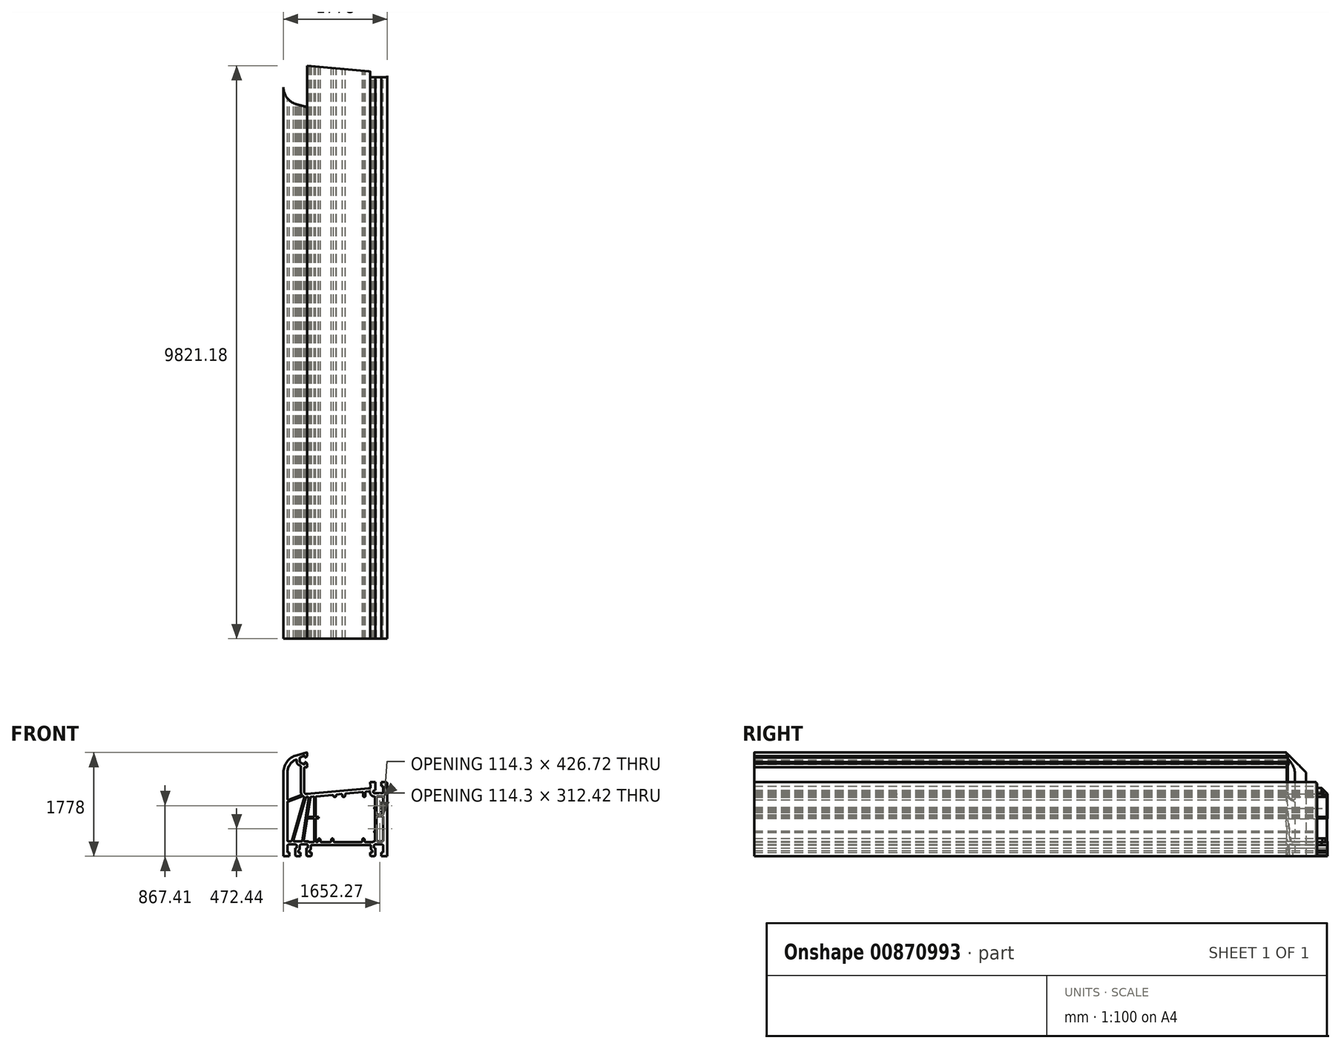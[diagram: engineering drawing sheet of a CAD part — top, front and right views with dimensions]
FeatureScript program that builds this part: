
annotation { "Feature Type Name" : "Feature", "Feature Type Description" : "" }
export const myFeature = defineFeature(function(context is Context, id is Id, definition is map)
    precondition{}
    {
        {
            var Q0;
            Q0=qCreatedBy(makeId("Front.planeOp"),FACE);
            var sketch = newSketch(context, id + "F0", { "sketchPlane" : qUnion([Q0])});
            skLineSegment(sketch, "E0", {"start": v(-889, -889) * mm, "end": v(-787.4, -889) * mm});
            skLineSegment(sketch, "E1", {"start": v(-508, 723.9) * mm, "end": v(-520.7, 723.9) * mm});
            skLineSegment(sketch, "E2", {"start": v(-520.7, 723.9) * mm, "end": v(-520.7, 701.04) * mm});
            skLineSegment(sketch, "E3", {"start": v(787.4, -889) * mm, "end": v(889, -889) * mm});
            skLineSegment(sketch, "E4", {"start": v(889, -889) * mm, "end": v(889, 355.6) * mm});
            skLineSegment(sketch, "E5", {"start": v(863.6, 381) * mm, "end": v(787.4, 381) * mm});
            skLineSegment(sketch, "E6", {"start": v(787.4, 381) * mm, "end": v(787.4, 314.96) * mm});
            skLineSegment(sketch, "E7", {"start": v(673.1, 241.3) * mm, "end": v(685.8, 241.3) * mm});
            skLineSegment(sketch, "E8", {"start": v(685.8, 241.3) * mm, "end": v(685.8, 381) * mm});
            skLineSegment(sketch, "E9", {"start": v(685.8, 381) * mm, "end": v(596.9, 381) * mm});
            skLineSegment(sketch, "E10", {"start": v(-889, 548.53) * mm, "end": v(-889, -889) * mm});
            skLineSegment(sketch, "E11", {"start": v(-482.6, 698.5) * mm, "end": v(-508, 723.9) * mm});
            skLineSegment(sketch, "E12", {"start": v(-482.6, 647.7) * mm, "end": v(-482.6, 698.5) * mm});
            skLineSegment(sketch, "E13", {"start": v(-520.7, 635) * mm, "end": v(-495.3, 635) * mm});
            skLineSegment(sketch, "E14", {"start": v(-589.28, 648.94) * mm, "end": v(-589.28, 635) * mm});
            skLineSegment(sketch, "E15", {"start": v(-623.74, 673.1) * mm, "end": v(-596.61, 660.45) * mm});
            skLineSegment(sketch, "E16", {"start": v(-660.4, 753.62) * mm, "end": v(-660.4, 730.65) * mm});
            skLineSegment(sketch, "E17", {"start": v(-820.42, 91.47) * mm, "end": v(-820.42, 548.53) * mm});
            skLineSegment(sketch, "E18", {"start": v(-812.06, 49.34) * mm, "end": v(-561.15, 140.67) * mm});
            skLineSegment(sketch, "E19", {"start": v(-820.42, -617.22) * mm, "end": v(-820.42, 37.41) * mm});
            skLineSegment(sketch, "E20", {"start": v(-587.31, 158.18) * mm, "end": v(-803.38, 79.54) * mm});
            skLineSegment(sketch, "E21", {"start": v(820.42, -215.9) * mm, "end": v(820.42, -617.22) * mm});
            skLineSegment(sketch, "E22", {"start": v(718.82, -203.2) * mm, "end": v(807.72, -203.2) * mm});
            skLineSegment(sketch, "E23", {"start": v(706.12, -617.22) * mm, "end": v(706.12, -215.9) * mm});
            skLineSegment(sketch, "E24", {"start": v(680.72, -495.3) * mm, "end": v(680.72, -618.92) * mm});
            skLineSegment(sketch, "E25", {"start": v(665.48, -482.6) * mm, "end": v(668.02, -482.6) * mm});
            skLineSegment(sketch, "E26", {"start": v(665.48, -457.2) * mm, "end": v(665.48, -482.6) * mm});
            skLineSegment(sketch, "E27", {"start": v(668.02, -457.2) * mm, "end": v(665.48, -457.2) * mm});
            skLineSegment(sketch, "E28", {"start": v(680.72, -88.9) * mm, "end": v(680.72, -444.5) * mm});
            skLineSegment(sketch, "E29", {"start": v(665.48, -76.2) * mm, "end": v(668.02, -76.2) * mm});
            skLineSegment(sketch, "E30", {"start": v(665.48, -50.8) * mm, "end": v(665.48, -76.2) * mm});
            skLineSegment(sketch, "E31", {"start": v(668.02, -50.8) * mm, "end": v(665.48, -50.8) * mm});
            skLineSegment(sketch, "E32", {"start": v(680.72, 122.06) * mm, "end": v(680.72, -38.1) * mm});
            skLineSegment(sketch, "E33", {"start": v(706.12, -165.1) * mm, "end": v(706.12, 121.92) * mm});
            skLineSegment(sketch, "E34", {"start": v(807.72, -177.8) * mm, "end": v(718.82, -177.8) * mm});
            skLineSegment(sketch, "E35", {"start": v(820.42, -152.4) * mm, "end": v(820.42, -165.1) * mm});
            skLineSegment(sketch, "E36", {"start": v(787.4, -139.7) * mm, "end": v(807.72, -139.7) * mm});
            skLineSegment(sketch, "E37", {"start": v(787.4, -114.3) * mm, "end": v(787.4, -139.7) * mm});
            skLineSegment(sketch, "E38", {"start": v(807.72, -114.3) * mm, "end": v(787.4, -114.3) * mm});
            skLineSegment(sketch, "E39", {"start": v(787.4, -88.9) * mm, "end": v(807.72, -88.9) * mm});
            skLineSegment(sketch, "E40", {"start": v(787.4, -63.5) * mm, "end": v(787.4, -88.9) * mm});
            skLineSegment(sketch, "E41", {"start": v(807.72, -63.5) * mm, "end": v(787.4, -63.5) * mm});
            skLineSegment(sketch, "E42", {"start": v(820.42, 121.92) * mm, "end": v(820.42, -50.8) * mm});
            skLineSegment(sketch, "E43", {"start": v(820.42, 314.96) * mm, "end": v(820.42, 215.9) * mm});
            skLineSegment(sketch, "E44", {"start": v(787.4, 314.96) * mm, "end": v(820.42, 314.96) * mm});
            skLineSegment(sketch, "E45", {"start": v(-520.7, 822.96) * mm, "end": v(-520.7, 800.1) * mm});
            skLineSegment(sketch, "E46", {"start": v(-602.27, 804.86) * mm, "end": v(-538.77, 834.47) * mm});
            skLineSegment(sketch, "E47", {"start": v(-609.6, 730.65) * mm, "end": v(-609.6, 793.35) * mm});
            skLineSegment(sketch, "E48", {"start": v(-538.77, 689.53) * mm, "end": v(-602.27, 719.14) * mm});
            skLineSegment(sketch, "E49", {"start": v(787.4, -822.96) * mm, "end": v(787.4, -889) * mm});
            skLineSegment(sketch, "E50", {"start": v(820.42, -822.96) * mm, "end": v(787.4, -822.96) * mm});
            skLineSegment(sketch, "E51", {"start": v(820.42, -711.2) * mm, "end": v(820.42, -822.96) * mm});
            skLineSegment(sketch, "E52", {"start": v(525.87, 217.04) * mm, "end": v(578.17, 221.93) * mm});
            skLineSegment(sketch, "E53", {"start": v(179.16, 184.6) * mm, "end": v(462.37, 211.1) * mm});
            skLineSegment(sketch, "E54", {"start": v(26.4, 170.31) * mm, "end": v(102.96, 177.48) * mm});
            skLineSegment(sketch, "E55", {"start": v(-323.76, 137.56) * mm, "end": v(-49.4, 163.22) * mm});
            skLineSegment(sketch, "E56", {"start": v(-417.58, 128.78) * mm, "end": v(-374.56, 132.8) * mm});
            skLineSegment(sketch, "E57", {"start": v(-486.55, 122.33) * mm, "end": v(-469.67, 123.9) * mm});
            skLineSegment(sketch, "E58", {"start": v(-589.28, 635) * mm, "end": v(-589.28, 215.9) * mm});
            skLineSegment(sketch, "E59", {"start": v(-533.4, 215.9) * mm, "end": v(-533.4, 622.3) * mm});
            skLineSegment(sketch, "E60", {"start": v(572.97, 277.57) * mm, "end": v(-491.75, 177.97) * mm});
            skLineSegment(sketch, "E61", {"start": v(795.02, 190.5) * mm, "end": v(673.1, 190.5) * mm});
            skLineSegment(sketch, "E62", {"start": v(718.82, 134.62) * mm, "end": v(807.72, 134.62) * mm});
            skLineSegment(sketch, "E63", {"start": v(-360.68, -248.92) * mm, "end": v(-360.68, -629.92) * mm});
            skLineSegment(sketch, "E64", {"start": v(-470.96, -236.22) * mm, "end": v(-373.38, -236.22) * mm});
            skLineSegment(sketch, "E65", {"start": v(-538.56, -615.34) * mm, "end": v(-483.52, -247.04) * mm});
            skLineSegment(sketch, "E66", {"start": v(-455.93, 109.39) * mm, "end": v(-564.8, -619.1) * mm});
            skLineSegment(sketch, "E67", {"start": v(-476.68, -201.32) * mm, "end": v(-428.96, 118.01) * mm});
            skLineSegment(sketch, "E68", {"start": v(-373.38, -215.9) * mm, "end": v(-464.12, -215.9) * mm});
            skLineSegment(sketch, "E69", {"start": v(-360.68, 120.16) * mm, "end": v(-360.68, -203.2) * mm});
            skLineSegment(sketch, "E70", {"start": v(-335.28, -203.2) * mm, "end": v(-335.28, 124.91) * mm});
            skLineSegment(sketch, "E71", {"start": v(-284.48, -215.9) * mm, "end": v(-322.58, -215.9) * mm});
            skLineSegment(sketch, "E72", {"start": v(-284.48, -241.3) * mm, "end": v(-284.48, -215.9) * mm});
            skLineSegment(sketch, "E73", {"start": v(-322.58, -241.3) * mm, "end": v(-284.48, -241.3) * mm});
            skLineSegment(sketch, "E74", {"start": v(-335.28, -629.92) * mm, "end": v(-335.28, -254) * mm});
            skLineSegment(sketch, "E75", {"start": v(167.64, 152.4) * mm, "end": v(167.64, 171.96) * mm});
            skLineSegment(sketch, "E76", {"start": v(116.84, 164.83) * mm, "end": v(116.84, 152.4) * mm});
            skLineSegment(sketch, "E77", {"start": v(593.11, 279.46) * mm, "end": v(572.97, 277.57) * mm});
            skLineSegment(sketch, "E78", {"start": v(604.58, 293.2) * mm, "end": v(596.9, 381) * mm});
            skLineSegment(sketch, "E79", {"start": v(-482.6, 825.5) * mm, "end": v(-482.6, 881.38) * mm});
            skLineSegment(sketch, "E80", {"start": v(-508, 800.1) * mm, "end": v(-482.6, 825.5) * mm});
            skLineSegment(sketch, "E81", {"start": v(-520.7, 800.1) * mm, "end": v(-508, 800.1) * mm});
            skLineSegment(sketch, "E82", {"start": v(-406.4, -876.3) * mm, "end": v(-406.4, -822.96) * mm});
            skLineSegment(sketch, "E83", {"start": v(-406.4, -822.96) * mm, "end": v(-444.5, -822.96) * mm});
            skLineSegment(sketch, "E84", {"start": v(-444.5, -822.96) * mm, "end": v(-444.5, -793.3) * mm});
            skLineSegment(sketch, "E85", {"start": v(-419.1, -749.3) * mm, "end": v(-419.1, -711.2) * mm});
            skLineSegment(sketch, "E86", {"start": v(-495.3, -876.3) * mm, "end": v(-482.6, -889) * mm});
            skLineSegment(sketch, "E87", {"start": v(-660.4, -749.3) * mm, "end": v(-685.8, -749.3) * mm});
            skLineSegment(sketch, "E88", {"start": v(-685.8, -749.3) * mm, "end": v(-685.8, -876.3) * mm});
            skLineSegment(sketch, "E89", {"start": v(-685.8, -876.3) * mm, "end": v(-673.1, -889) * mm});
            skLineSegment(sketch, "E90", {"start": v(-673.1, -889) * mm, "end": v(-596.9, -889) * mm});
            skLineSegment(sketch, "E91", {"start": v(-596.9, -889) * mm, "end": v(-596.9, -822.96) * mm});
            skLineSegment(sketch, "E92", {"start": v(-596.9, -822.96) * mm, "end": v(-635, -822.96) * mm});
            skLineSegment(sketch, "E93", {"start": v(-635, -822.96) * mm, "end": v(-635, -793.3) * mm});
            skLineSegment(sketch, "E94", {"start": v(-609.6, -749.3) * mm, "end": v(-609.6, -711.2) * mm});
            skLineSegment(sketch, "E95", {"start": v(-660.4, -711.2) * mm, "end": v(-660.4, -749.3) * mm});
            skLineSegment(sketch, "E96", {"start": v(596.9, -822.96) * mm, "end": v(596.9, -876.3) * mm});
            skLineSegment(sketch, "E97", {"start": v(635, -822.96) * mm, "end": v(596.9, -822.96) * mm});
            skLineSegment(sketch, "E98", {"start": v(635, -793.3) * mm, "end": v(635, -822.96) * mm});
            skLineSegment(sketch, "E99", {"start": v(609.6, -711.2) * mm, "end": v(609.6, -749.3) * mm});
            skLineSegment(sketch, "E100", {"start": v(-257.8, -629.92) * mm, "end": v(-257.8, -603.25) * mm});
            skLineSegment(sketch, "E101", {"start": v(-295.9, -603.25) * mm, "end": v(-295.9, -629.92) * mm});
            skLineSegment(sketch, "E102", {"start": v(-31.75, -629.92) * mm, "end": v(-31.75, -603.25) * mm});
            skLineSegment(sketch, "E103", {"start": v(-69.85, -603.25) * mm, "end": v(-69.85, -629.92) * mm});
            skLineSegment(sketch, "E104", {"start": v(499.11, -629.92) * mm, "end": v(499.11, -603.25) * mm});
            skLineSegment(sketch, "E105", {"start": v(461.01, -603.25) * mm, "end": v(461.01, -629.92) * mm});
            skLineSegment(sketch, "E106", {"start": v(-495.3, -749.3) * mm, "end": v(-495.3, -876.3) * mm});
            skLineSegment(sketch, "E107", {"start": v(-469.9, -749.3) * mm, "end": v(-495.3, -749.3) * mm});
            skLineSegment(sketch, "E108", {"start": v(-469.9, -711.2) * mm, "end": v(-469.9, -749.3) * mm});
            skLineSegment(sketch, "E109", {"start": v(-482.6, -889) * mm, "end": v(-419.1, -889) * mm});
            skLineSegment(sketch, "E110", {"start": v(-419.1, -889) * mm, "end": v(-406.4, -876.3) * mm});
            skLineSegment(sketch, "E111", {"start": v(-820.42, -822.96) * mm, "end": v(-820.42, -711.2) * mm});
            skLineSegment(sketch, "E112", {"start": v(-787.4, -822.96) * mm, "end": v(-820.42, -822.96) * mm});
            skLineSegment(sketch, "E113", {"start": v(-787.4, -889) * mm, "end": v(-787.4, -822.96) * mm});
            skLineSegment(sketch, "E114", {"start": v(-492.2, 888.74) * mm, "end": v(-663.09, 842.95) * mm});
            skLineSegment(sketch, "E115", {"start": v(476.25, 198.46) * mm, "end": v(476.25, 146.05) * mm});
            skLineSegment(sketch, "E116", {"start": v(514.35, 146.05) * mm, "end": v(514.35, 204.4) * mm});
            skLineSegment(sketch, "E117", {"start": v(-718.23, -613.72) * mm, "end": v(-509.92, 112.75) * mm});
            skLineSegment(sketch, "E118", {"start": v(-534.56, 118.96) * mm, "end": v(-746.66, -620.72) * mm});
            skLineSegment(sketch, "E119", {"start": v(660.4, -749.3) * mm, "end": v(660.4, -711.2) * mm});
            skLineSegment(sketch, "E120", {"start": v(685.8, -749.3) * mm, "end": v(660.4, -749.3) * mm});
            skLineSegment(sketch, "E121", {"start": v(685.8, -876.3) * mm, "end": v(685.8, -749.3) * mm});
            skLineSegment(sketch, "E122", {"start": v(673.1, -889) * mm, "end": v(685.8, -876.3) * mm});
            skLineSegment(sketch, "E123", {"start": v(609.6, -889) * mm, "end": v(673.1, -889) * mm});
            skLineSegment(sketch, "E124", {"start": v(596.9, -876.3) * mm, "end": v(609.6, -889) * mm});
            skLineSegment(sketch, "E125", {"start": v(-758.87, -629.92) * mm, "end": v(-807.72, -629.92) * mm});
            skLineSegment(sketch, "E126", {"start": v(-577.36, -629.92) * mm, "end": v(-706.02, -629.92) * mm});
            skLineSegment(sketch, "E127", {"start": v(-495.3, -629.92) * mm, "end": v(-526, -629.92) * mm});
            skLineSegment(sketch, "E128", {"start": v(-373.38, -642.62) * mm, "end": v(-448.12, -642.62) * mm});
            skLineSegment(sketch, "E129", {"start": v(-308.6, -642.62) * mm, "end": v(-322.58, -642.62) * mm});
            skLineSegment(sketch, "E130", {"start": v(-82.55, -642.62) * mm, "end": v(-245.1, -642.62) * mm});
            skLineSegment(sketch, "E131", {"start": v(448.31, -642.62) * mm, "end": v(-19.05, -642.62) * mm});
            skLineSegment(sketch, "E132", {"start": v(638.62, -642.62) * mm, "end": v(511.81, -642.62) * mm});
            skLineSegment(sketch, "E133", {"start": v(807.72, -629.92) * mm, "end": v(718.82, -629.92) * mm});
            skLineSegment(sketch, "E134", {"start": v(685.8, -685.8) * mm, "end": v(795.02, -685.8) * mm});
            skLineSegment(sketch, "E135", {"start": v(-406.4, -698.5) * mm, "end": v(596.9, -698.5) * mm});
            skLineSegment(sketch, "E136", {"start": v(-584.2, -685.8) * mm, "end": v(-495.3, -685.8) * mm});
            skLineSegment(sketch, "E137", {"start": v(-795.02, -685.8) * mm, "end": v(-685.8, -685.8) * mm});
            skArc(sketch, "E138", {"start": v(-663.09, 842.95) * mm, "mid": v(-826.01, 734.09) * mm, "end": v(-889, 548.53) * mm});
            skArc(sketch, "E139", {"start": v(604.58, 293.2) * mm, "mid": v(601.68, 283.97) * mm, "end": v(593.11, 279.46) * mm});
            skArc(sketch, "E140", {"start": v(647.76, 214.11) * mm, "mid": v(654.52, 233.22) * mm, "end": v(673.1, 241.3) * mm});
            skArc(sketch, "E141", {"start": v(514.35, 204.4) * mm, "mid": v(517.66, 212.95) * mm, "end": v(525.87, 217.04) * mm});
            skArc(sketch, "E142", {"start": v(462.37, 211.1) * mm, "mid": v(472.1, 207.84) * mm, "end": v(476.25, 198.46) * mm});
            skArc(sketch, "E143", {"start": v(476.25, 146.05) * mm, "mid": v(495.3, 127) * mm, "end": v(514.35, 146.05) * mm});
            skArc(sketch, "E144", {"start": v(-49.4, 163.22) * mm, "mid": v(-39.9, 160.17) * mm, "end": v(-35.53, 151.19) * mm});
            skArc(sketch, "E145", {"start": v(15, 155.91) * mm, "mid": v(17.61, 165.55) * mm, "end": v(26.4, 170.31) * mm});
            skArc(sketch, "E146", {"start": v(-35.53, 151.19) * mm, "mid": v(-7.8, 127.11) * mm, "end": v(15, 155.91) * mm});
            skArc(sketch, "E147", {"start": v(-706.02, -629.92) * mm, "mid": v(-716.17, -624.86) * mm, "end": v(-718.23, -613.72) * mm});
            skArc(sketch, "E148", {"start": v(-509.92, 112.75) * mm, "mid": v(-505.24, 119.48) * mm, "end": v(-497.42, 121.94) * mm});
            skArc(sketch, "E149", {"start": v(-540.64, 133.58) * mm, "mid": v(-535.04, 127.33) * mm, "end": v(-534.56, 118.96) * mm});
            skArc(sketch, "E150", {"start": v(-746.66, -620.72) * mm, "mid": v(-751.23, -627.36) * mm, "end": v(-758.87, -629.92) * mm});
            skArc(sketch, "E151", {"start": v(660.4, -711.2) * mm, "mid": v(661.27, -704.63) * mm, "end": v(663.8, -698.5) * mm});
            skArc(sketch, "E152", {"start": v(609.6, -749.3) * mm, "mid": v(616.4, -774.7) * mm, "end": v(635, -793.3) * mm});
            skArc(sketch, "E153", {"start": v(596.9, -698.5) * mm, "mid": v(605.88, -702.22) * mm, "end": v(609.6, -711.2) * mm});
            skArc(sketch, "E154", {"start": v(-807.72, -629.92) * mm, "mid": v(-816.7, -626.2) * mm, "end": v(-820.42, -617.22) * mm});
            skArc(sketch, "E155", {"start": v(-454.5, -640.9) * mm, "mid": v(-474.17, -632.71) * mm, "end": v(-495.3, -629.92) * mm});
            skArc(sketch, "E156", {"start": v(-448.12, -642.62) * mm, "mid": v(-451.42, -642.18) * mm, "end": v(-454.5, -640.9) * mm});
            skArc(sketch, "E157", {"start": v(645, -640.9) * mm, "mid": v(641.92, -642.18) * mm, "end": v(638.62, -642.62) * mm});
            skArc(sketch, "E158", {"start": v(670.42, -631.39) * mm, "mid": v(657.3, -635.08) * mm, "end": v(645, -640.9) * mm});
            skArc(sketch, "E159", {"start": v(820.42, -617.22) * mm, "mid": v(816.7, -626.2) * mm, "end": v(807.72, -629.92) * mm});
            skArc(sketch, "E160", {"start": v(795.02, -685.8) * mm, "mid": v(812.98, -693.24) * mm, "end": v(820.42, -711.2) * mm});
            skArc(sketch, "E161", {"start": v(-495.3, -685.8) * mm, "mid": v(-482.6, -689.2) * mm, "end": v(-473.3, -698.5) * mm});
            skArc(sketch, "E162", {"start": v(-820.42, -711.2) * mm, "mid": v(-812.98, -693.24) * mm, "end": v(-795.02, -685.8) * mm});
            skArc(sketch, "E163", {"start": v(663.8, -698.5) * mm, "mid": v(673.1, -689.2) * mm, "end": v(685.8, -685.8) * mm});
            skArc(sketch, "E164", {"start": v(-69.85, -629.92) * mm, "mid": v(-73.57, -638.9) * mm, "end": v(-82.55, -642.62) * mm});
            skArc(sketch, "E165", {"start": v(-31.75, -603.25) * mm, "mid": v(-50.8, -584.2) * mm, "end": v(-69.85, -603.25) * mm});
            skArc(sketch, "E166", {"start": v(-19.05, -642.62) * mm, "mid": v(-28.03, -638.9) * mm, "end": v(-31.75, -629.92) * mm});
            skArc(sketch, "E167", {"start": v(-245.1, -642.62) * mm, "mid": v(-254.1, -638.9) * mm, "end": v(-257.8, -629.92) * mm});
            skArc(sketch, "E168", {"start": v(-257.8, -603.25) * mm, "mid": v(-276.86, -584.2) * mm, "end": v(-295.9, -603.25) * mm});
            skArc(sketch, "E169", {"start": v(-295.9, -629.92) * mm, "mid": v(-299.63, -638.9) * mm, "end": v(-308.6, -642.62) * mm});
            skArc(sketch, "E170", {"start": v(511.81, -642.62) * mm, "mid": v(502.83, -638.9) * mm, "end": v(499.11, -629.92) * mm});
            skArc(sketch, "E171", {"start": v(499.11, -603.25) * mm, "mid": v(480.06, -584.2) * mm, "end": v(461.01, -603.25) * mm});
            skArc(sketch, "E172", {"start": v(461.01, -629.92) * mm, "mid": v(457.3, -638.9) * mm, "end": v(448.31, -642.62) * mm});
            skArc(sketch, "E173", {"start": v(-473.3, -698.5) * mm, "mid": v(-470.77, -704.63) * mm, "end": v(-469.9, -711.2) * mm});
            skArc(sketch, "E174", {"start": v(-444.5, -793.3) * mm, "mid": v(-425.9, -774.7) * mm, "end": v(-419.1, -749.3) * mm});
            skArc(sketch, "E175", {"start": v(-419.1, -711.2) * mm, "mid": v(-415.38, -702.22) * mm, "end": v(-406.4, -698.5) * mm});
            skArc(sketch, "E176", {"start": v(-685.8, -685.8) * mm, "mid": v(-667.84, -693.24) * mm, "end": v(-660.4, -711.2) * mm});
            skArc(sketch, "E177", {"start": v(-635, -793.3) * mm, "mid": v(-616.4, -774.7) * mm, "end": v(-609.6, -749.3) * mm});
            skArc(sketch, "E178", {"start": v(-609.6, -711.2) * mm, "mid": v(-602.16, -693.24) * mm, "end": v(-584.2, -685.8) * mm});
            skArc(sketch, "E179", {"start": v(-482.6, 881.38) * mm, "mid": v(-485.58, 887.43) * mm, "end": v(-492.2, 888.74) * mm});
            skArc(sketch, "E180", {"start": v(-538.77, 834.47) * mm, "mid": v(-526.58, 833.67) * mm, "end": v(-520.7, 822.96) * mm});
            skArc(sketch, "E181", {"start": v(-609.6, 793.35) * mm, "mid": v(-607.61, 800.17) * mm, "end": v(-602.27, 804.86) * mm});
            skArc(sketch, "E182", {"start": v(-602.27, 719.14) * mm, "mid": v(-607.61, 723.83) * mm, "end": v(-609.6, 730.65) * mm});
            skArc(sketch, "E183", {"start": v(-520.7, 701.04) * mm, "mid": v(-526.58, 690.33) * mm, "end": v(-538.77, 689.53) * mm});
            skArc(sketch, "E184", {"start": v(-495.3, 635) * mm, "mid": v(-486.32, 638.72) * mm, "end": v(-482.6, 647.7) * mm});
            skArc(sketch, "E185", {"start": v(-596.61, 660.45) * mm, "mid": v(-591.27, 655.77) * mm, "end": v(-589.28, 648.94) * mm});
            skArc(sketch, "E186", {"start": v(-660.4, 730.65) * mm, "mid": v(-650.46, 696.53) * mm, "end": v(-623.74, 673.1) * mm});
            skArc(sketch, "E187", {"start": v(-678.15, 765.27) * mm, "mid": v(-666.13, 764.23) * mm, "end": v(-660.4, 753.62) * mm});
            skArc(sketch, "E188", {"start": v(-820.42, 548.53) * mm, "mid": v(-781.68, 678.16) * mm, "end": v(-678.15, 765.27) * mm});
            skArc(sketch, "E189", {"start": v(-561.15, 140.67) * mm, "mid": v(-555.13, 141.32) * mm, "end": v(-549.48, 139.11) * mm});
            skArc(sketch, "E190", {"start": v(-820.42, 37.41) * mm, "mid": v(-818.12, 44.7) * mm, "end": v(-812.06, 49.34) * mm});
            skArc(sketch, "E191", {"start": v(-803.38, 79.54) * mm, "mid": v(-815, 81.07) * mm, "end": v(-820.42, 91.47) * mm});
            skArc(sketch, "E192", {"start": v(-580.18, 175.56) * mm, "mid": v(-579.9, 165.3) * mm, "end": v(-587.31, 158.18) * mm});
            skArc(sketch, "E193", {"start": v(807.72, -203.2) * mm, "mid": v(816.7, -206.92) * mm, "end": v(820.42, -215.9) * mm});
            skArc(sketch, "E194", {"start": v(706.12, -215.9) * mm, "mid": v(709.84, -206.92) * mm, "end": v(718.82, -203.2) * mm});
            skArc(sketch, "E195", {"start": v(718.82, -629.92) * mm, "mid": v(709.84, -626.2) * mm, "end": v(706.12, -617.22) * mm});
            skArc(sketch, "E196", {"start": v(680.72, -618.92) * mm, "mid": v(677.81, -627) * mm, "end": v(670.42, -631.39) * mm});
            skArc(sketch, "E197", {"start": v(668.02, -482.6) * mm, "mid": v(677, -486.32) * mm, "end": v(680.72, -495.3) * mm});
            skArc(sketch, "E198", {"start": v(680.72, -444.5) * mm, "mid": v(677, -453.48) * mm, "end": v(668.02, -457.2) * mm});
            skArc(sketch, "E199", {"start": v(668.02, -76.2) * mm, "mid": v(677, -79.92) * mm, "end": v(680.72, -88.9) * mm});
            skArc(sketch, "E200", {"start": v(680.72, -38.1) * mm, "mid": v(677, -47.08) * mm, "end": v(668.02, -50.8) * mm});
            skArc(sketch, "E201", {"start": v(668.7, 134.74) * mm, "mid": v(677.24, 130.8) * mm, "end": v(680.72, 122.06) * mm});
            skArc(sketch, "E202", {"start": v(706.12, 121.92) * mm, "mid": v(709.84, 130.9) * mm, "end": v(718.82, 134.62) * mm});
            skArc(sketch, "E203", {"start": v(718.82, -177.8) * mm, "mid": v(709.84, -174.08) * mm, "end": v(706.12, -165.1) * mm});
            skArc(sketch, "E204", {"start": v(820.42, -165.1) * mm, "mid": v(816.7, -174.08) * mm, "end": v(807.72, -177.8) * mm});
            skArc(sketch, "E205", {"start": v(807.72, -139.7) * mm, "mid": v(816.7, -143.42) * mm, "end": v(820.42, -152.4) * mm});
            skArc(sketch, "E206", {"start": v(820.42, -101.6) * mm, "mid": v(816.7, -110.58) * mm, "end": v(807.72, -114.3) * mm});
            skArc(sketch, "E207", {"start": v(807.72, -88.9) * mm, "mid": v(816.7, -92.62) * mm, "end": v(820.42, -101.6) * mm});
            skArc(sketch, "E208", {"start": v(820.42, -50.8) * mm, "mid": v(816.7, -59.78) * mm, "end": v(807.72, -63.5) * mm});
            skArc(sketch, "E209", {"start": v(889, 355.6) * mm, "mid": v(881.56, 373.56) * mm, "end": v(863.6, 381) * mm});
            skArc(sketch, "E210", {"start": v(807.72, 134.62) * mm, "mid": v(816.7, 130.9) * mm, "end": v(820.42, 121.92) * mm});
            skArc(sketch, "E211", {"start": v(578.17, 221.93) * mm, "mid": v(587.57, 218.97) * mm, "end": v(592.02, 210.18) * mm});
            skArc(sketch, "E212", {"start": v(-497.42, 121.94) * mm, "mid": v(-491.98, 121.98) * mm, "end": v(-486.55, 122.33) * mm});
            skArc(sketch, "E213", {"start": v(-549.48, 139.11) * mm, "mid": v(-545.14, 136.22) * mm, "end": v(-540.64, 133.58) * mm});
            skArc(sketch, "E214", {"start": v(-589.28, 215.9) * mm, "mid": v(-586.98, 195.23) * mm, "end": v(-580.18, 175.56) * mm});
            skArc(sketch, "E215", {"start": v(-533.4, 622.3) * mm, "mid": v(-529.68, 631.28) * mm, "end": v(-520.7, 635) * mm});
            skArc(sketch, "E216", {"start": v(-491.75, 177.97) * mm, "mid": v(-520.96, 187.73) * mm, "end": v(-533.4, 215.9) * mm});
            skArc(sketch, "E217", {"start": v(673.1, 190.5) * mm, "mid": v(655.78, 197.32) * mm, "end": v(647.76, 214.11) * mm});
            skArc(sketch, "E218", {"start": v(820.42, 215.9) * mm, "mid": v(812.98, 197.94) * mm, "end": v(795.02, 190.5) * mm});
            skArc(sketch, "E219", {"start": v(592.02, 210.18) * mm, "mid": v(616.1, 157.96) * mm, "end": v(668.7, 134.74) * mm});
            skArc(sketch, "E220", {"start": v(-360.68, -629.92) * mm, "mid": v(-364.4, -638.9) * mm, "end": v(-373.38, -642.62) * mm});
            skArc(sketch, "E221", {"start": v(-373.38, -236.22) * mm, "mid": v(-364.4, -239.94) * mm, "end": v(-360.68, -248.92) * mm});
            skArc(sketch, "E222", {"start": v(-483.52, -247.04) * mm, "mid": v(-479.25, -239.3) * mm, "end": v(-470.96, -236.22) * mm});
            skArc(sketch, "E223", {"start": v(-526, -629.92) * mm, "mid": v(-535.62, -625.51) * mm, "end": v(-538.56, -615.34) * mm});
            skArc(sketch, "E224", {"start": v(-564.8, -619.1) * mm, "mid": v(-569.07, -626.84) * mm, "end": v(-577.36, -629.92) * mm});
            skArc(sketch, "E225", {"start": v(-469.67, 123.9) * mm, "mid": v(-459.27, 120) * mm, "end": v(-455.93, 109.39) * mm});
            skArc(sketch, "E226", {"start": v(-428.96, 118.01) * mm, "mid": v(-425.13, 125.36) * mm, "end": v(-417.58, 128.78) * mm});
            skArc(sketch, "E227", {"start": v(-464.12, -215.9) * mm, "mid": v(-473.74, -211.5) * mm, "end": v(-476.68, -201.32) * mm});
            skArc(sketch, "E228", {"start": v(-360.68, -203.2) * mm, "mid": v(-364.4, -212.18) * mm, "end": v(-373.38, -215.9) * mm});
            skArc(sketch, "E229", {"start": v(-374.56, 132.8) * mm, "mid": v(-364.83, 129.55) * mm, "end": v(-360.68, 120.16) * mm});
            skArc(sketch, "E230", {"start": v(-335.28, 124.91) * mm, "mid": v(-331.97, 133.46) * mm, "end": v(-323.76, 137.56) * mm});
            skArc(sketch, "E231", {"start": v(-322.58, -215.9) * mm, "mid": v(-331.56, -212.18) * mm, "end": v(-335.28, -203.2) * mm});
            skArc(sketch, "E232", {"start": v(-322.58, -642.62) * mm, "mid": v(-331.56, -638.9) * mm, "end": v(-335.28, -629.92) * mm});
            skArc(sketch, "E233", {"start": v(-335.28, -254) * mm, "mid": v(-331.56, -245.02) * mm, "end": v(-322.58, -241.3) * mm});
            skArc(sketch, "E234", {"start": v(167.64, 171.96) * mm, "mid": v(170.95, 180.51) * mm, "end": v(179.16, 184.6) * mm});
            skArc(sketch, "E235", {"start": v(102.96, 177.48) * mm, "mid": v(112.7, 174.22) * mm, "end": v(116.84, 164.83) * mm});
            skArc(sketch, "E236", {"start": v(116.84, 152.4) * mm, "mid": v(142.24, 127) * mm, "end": v(167.64, 152.4) * mm});
            skSolve(sketch);
        }
        {
            var Q0;
            Q0 = qSketchRegion(id + "F0", true);
            extrude(context, id + "F1", {"entities" : qUnion([Q0]), "depth" : 10000 * mm, "offsetDistance" : 25 * mm});
        }
        {
            var Q0;
            Q0=makeQuery(id+"F1.opExtrude","SWEPT_FACE",FACE,{"disambiguationData":[OSD([sQuery(id+"F0.wireOp",EDGE,"E135")])]});
            var sketch = newSketch(context, id + "F2", { "sketchPlane" : qUnion([Q0])});
            skLineSegment(sketch, "E237", {"start": v(889, 0) * mm, "end": v(889, 355.6) * mm});
            skLineSegment(sketch, "E238", {"start": v(863.6, 381) * mm, "end": v(787.4, 381) * mm});
            skLineSegment(sketch, "E239", {"start": v(-889, 548.53) * mm, "end": v(-889, 0) * mm});
            skLineSegment(sketch, "E240", {"start": v(-482.6, 647.7) * mm, "end": v(-482.6, 698.5) * mm});
            skLineSegment(sketch, "E241", {"start": v(572.97, 277.57) * mm, "end": v(-482.6, 178.82) * mm});
            skLineSegment(sketch, "E242", {"start": v(593.11, 279.46) * mm, "end": v(572.97, 277.57) * mm});
            skLineSegment(sketch, "E243", {"start": v(-482.6, 825.5) * mm, "end": v(-482.6, 881.38) * mm});
            skLineSegment(sketch, "E244", {"start": v(-492.2, 888.74) * mm, "end": v(-663.09, 842.95) * mm});
            skArc(sketch, "E245", {"start": v(-663.09, 842.95) * mm, "mid": v(-826.01, 734.09) * mm, "end": v(-889, 548.53) * mm});
            skArc(sketch, "E246", {"start": v(-482.6, 881.38) * mm, "mid": v(-485.58, 887.43) * mm, "end": v(-492.2, 888.74) * mm});
            skArc(sketch, "E247", {"start": v(889, 355.6) * mm, "mid": v(881.56, 373.56) * mm, "end": v(863.6, 381) * mm});
            skArc(sketch, "E248", {"start": v(596.9, 280.41) * mm, "mid": v(595.04, 279.79) * mm, "end": v(593.11, 279.46) * mm});
            skLineSegment(sketch, "E249", {"start": v(596.9, 381) * mm, "end": v(787.4, 381) * mm});
            skLineSegment(sketch, "E250", {"start": v(-482.6, 825.5) * mm, "end": v(-482.6, 178.82) * mm});
            skLineSegment(sketch, "E251", {"start": v(-889, 0) * mm, "end": v(889, 0) * mm});
            skLineSegment(sketch, "E252", {"start": v(596.9, 381) * mm, "end": v(596.9, 280.41) * mm});
            skSolve(sketch);
        }
        {
            var Q0;
            Q0 = qSketchRegion(id + "F2", true);
            extrude(context, id + "F3", {"entities" : qUnion([Q0]), "operationType" : NewBodyOperationType.REMOVE, "endBound" : BoundingType.SYMMETRIC, "oppositeDirection" : true, "depth" : 9000 * mm, "offsetDistance" : 25 * mm});
        }
    });
